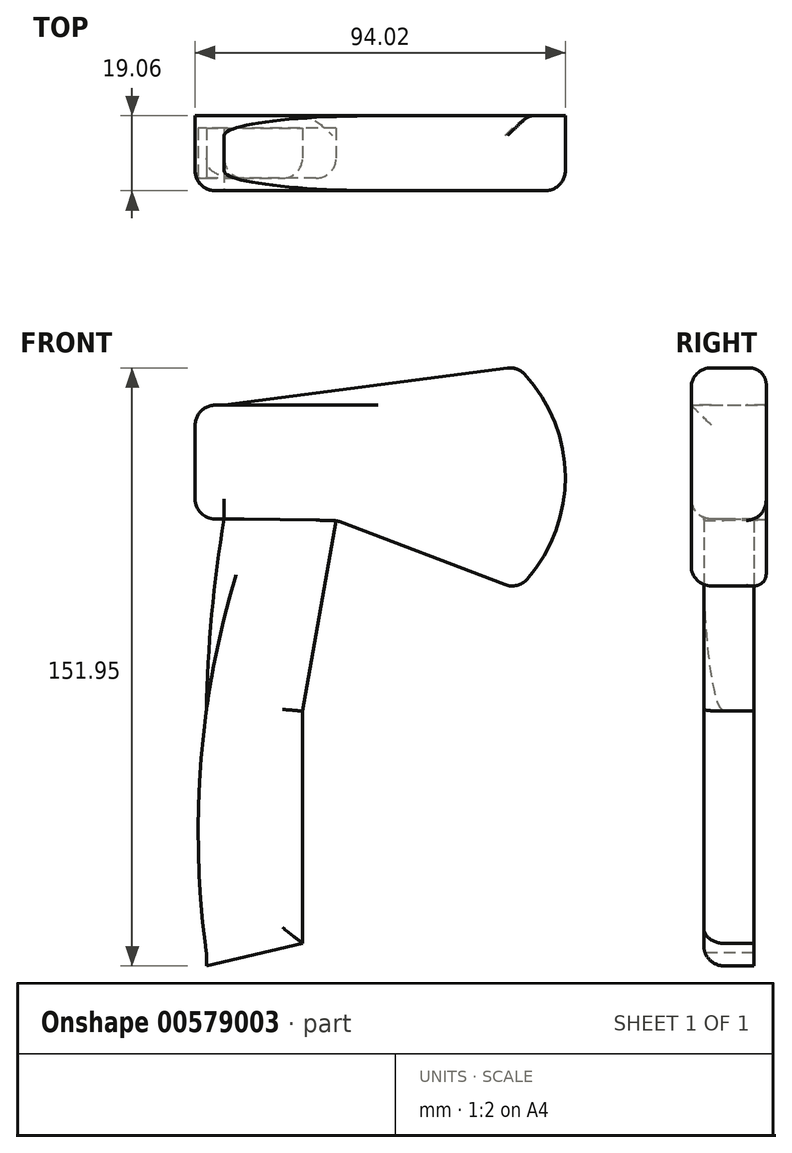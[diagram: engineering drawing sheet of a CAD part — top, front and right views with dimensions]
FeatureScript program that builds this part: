
annotation { "Feature Type Name" : "Feature", "Feature Type Description" : "" }
export const myFeature = defineFeature(function(context is Context, id is Id, definition is map)
    precondition{}
    {
        {
            var Q0;
            Q0=qCreatedBy(makeId("Front.planeOp"),FACE);
            var sketch = newSketch(context, id + "F0", { "sketchPlane" : qUnion([Q0])});
            skArc(sketch, "E0", {"start": v(-13.8, -11.12) * mm, "mid": v(-15.9, -41.85) * mm, "end": v(-13.8, -72.58) * mm});
            skLineSegment(sketch, "E1", {"start": v(-13.8, -72.58) * mm, "end": v(-13.8, -75.84) * mm});
            skArc(sketch, "E2", {"start": v(-9.33, 37.72) * mm, "mid": v(-12.45, 13.38) * mm, "end": v(-13.8, -11.12) * mm});
            skLineSegment(sketch, "E3", {"start": v(-9.33, 37.72) * mm, "end": v(-16.65, 37.72) * mm});
            skLineSegment(sketch, "E4", {"start": v(-16.65, 37.72) * mm, "end": v(-16.65, 66.62) * mm});
            skLineSegment(sketch, "E5", {"start": v(-16.65, 66.62) * mm, "end": v(-9.33, 66.62) * mm});
            skLineSegment(sketch, "E6", {"start": v(-9.33, 66.62) * mm, "end": v(65.16, 76.39) * mm});
            skLineSegment(sketch, "E7", {"start": v(19.16, 37.32) * mm, "end": v(65.16, 19.81) * mm});
            skLineSegment(sketch, "E8", {"start": v(-13.8, -75.84) * mm, "end": v(10.62, -70.14) * mm});
            skArc(sketch, "E9", {"start": v(65.16, 19.81) * mm, "mid": v(77.37, 48.1) * mm, "end": v(65.16, 76.39) * mm});
            skLineSegment(sketch, "E10", {"start": v(19.16, 37.32) * mm, "end": v(-9.33, 37.72) * mm});
            skLineSegment(sketch, "E11", {"start": v(-9.33, 66.62) * mm, "end": v(-9.33, 37.72) * mm});
            skLineSegment(sketch, "E12", {"start": v(19.16, 37.32) * mm, "end": v(19.16, 70.36) * mm});
            skLineSegment(sketch, "E13", {"start": v(10.62, -11.12) * mm, "end": v(-13.8, -11.12) * mm});
            skLineSegment(sketch, "E14", {"start": v(-1.6, -72.99) * mm, "end": v(0, -11.12) * mm});
            skLineSegment(sketch, "E15", {"start": v(19.16, 37.32) * mm, "end": v(10.62, -11.12) * mm});
            skLineSegment(sketch, "E16", {"start": v(10.62, -70.14) * mm, "end": v(10.62, -11.12) * mm});
            skLineSegment(sketch, "E17", {"start": v(0, -11.12) * mm, "end": v(4.92, 37.52) * mm});
            skSolve(sketch);
        }
        {
            var Q0;
            {var subQ1=sQuery(id+"F0.wireOp",EDGE,"E0");Q0=makeQuery(id+"F0.imprint","IMPRINT",FACE,{"disambiguationData":[TD([[makeQuery(id+"F0.imprint","IMPRINT",EDGE,{"derivedFrom":subQ1}),1.0]])]});}
            var Q1;
            {var subQ2=sQuery(id+"F0.wireOp",EDGE,"E14");Q1=makeQuery(id+"F0.imprint","IMPRINT",FACE,{"disambiguationData":[TD([[makeQuery(id+"F0.imprint","IMPRINT",EDGE,{"derivedFrom":subQ2}),-1.0]])]});}
            var Q2;
            {var subQ0=sQuery(id+"F0.wireOp",EDGE,"E2");Q2=makeQuery(id+"F0.imprint","IMPRINT",FACE,{"disambiguationData":[TD([[makeQuery(id+"F0.imprint","IMPRINT",EDGE,{"derivedFrom":subQ0}),1.0]])]});}
            var Q3;
            {var subQ0=sQuery(id+"F0.wireOp",EDGE,"E15");Q3=makeQuery(id+"F0.imprint","IMPRINT",FACE,{"disambiguationData":[TD([[makeQuery(id+"F0.imprint","IMPRINT",EDGE,{"derivedFrom":subQ0}),-1.0]])]});}
            extrude(context, id + "F1", {"entities" : qUnion([Q0, Q1, Q2, Q3]), "endBound" : BoundingType.SYMMETRIC, "oppositeDirection" : true, "depth" : 12.7 * mm, "offsetDistance" : 25.4 * mm});
        }
        {
            var Q0;
            Q0=makeQuery(id+"F0.imprint","IMPRINT",FACE,{"disambiguationData":[TD([[makeQuery(id+"F0.imprint","IMPRINT",EDGE,{"derivedFrom":sQuery(id+"F0.wireOp",EDGE,"E3")}),-1.0]])]});
            var Q1;
            {var subQ0=sQuery(id+"F0.wireOp",EDGE,"E11");Q1=makeQuery(id+"F0.imprint","IMPRINT",FACE,{"disambiguationData":[TD([[makeQuery(id+"F0.imprint","IMPRINT",EDGE,{"derivedFrom":subQ0}),1.0]])]});}
            var Q2;
            {var subQ0=sQuery(id+"F0.wireOp",EDGE,"E12");Q2=makeQuery(id+"F0.imprint","IMPRINT",FACE,{"disambiguationData":[TD([[makeQuery(id+"F0.imprint","IMPRINT",EDGE,{"derivedFrom":subQ0}),-1.0]])]});}
            extrude(context, id + "F2", {"entities" : qUnion([Q0, Q1, Q2]), "endBound" : BoundingType.SYMMETRIC, "depth" : 19.05 * mm, "offsetDistance" : 25.4 * mm});
        }
        {
            var Q0;
            Q0=makeQuery(id+"F1.opExtrude","CAP_EDGE",EDGE,{"disambiguationData":[OSD([sQuery(id+"F0.wireOp",EDGE,"E15")])],"isStart":true});
            var Q1;
            Q1=makeQuery(id+"F1.opExtrude","CAP_EDGE",EDGE,{"disambiguationData":[OSD([sQuery(id+"F0.wireOp",EDGE,"E16")])],"isStart":true});
            var Q2;
            Q2=makeQuery(id+"F1.opExtrude","CAP_EDGE",EDGE,{"disambiguationData":[OSD([sQuery(id+"F0.wireOp",EDGE,"E2")])],"isStart":true});
            var Q3;
            Q3=makeQuery(id+"F1.opExtrude","CAP_EDGE",EDGE,{"disambiguationData":[OSD([sQuery(id+"F0.wireOp",EDGE,"E8")])],"isStart":true});
            var Q4;
            Q4=makeQuery(id+"F2.opExtrude","CAP_EDGE",EDGE,{"disambiguationData":[OSD([sQuery(id+"F0.wireOp",EDGE,"E10")])],"isStart":false});
            var Q5;
            Q5=makeQuery(id+"F2.opExtrude","SWEPT_EDGE",EDGE,{"disambiguationData":[OSD([sQuery(id+"F0.wireOp",EDGE,"E3"),sQuery(id+"F0.wireOp",EDGE,"E4")])]});
            var Q6;
            Q6=makeQuery(id+"F2.opExtrude","CAP_EDGE",EDGE,{"disambiguationData":[OSD([sQuery(id+"F0.wireOp",EDGE,"E9")])],"isStart":false});
            var Q7;
            Q7=makeQuery(id+"F2.opExtrude","SWEPT_FACE",FACE,{"disambiguationData":[OSD([sQuery(id+"F0.wireOp",EDGE,"E7")])]});
            var Q8;
            Q8=makeQuery(id+"F2.opExtrude","CAP_EDGE",EDGE,{"disambiguationData":[OSD([sQuery(id+"F0.wireOp",EDGE,"E4")])],"isStart":false});
            var Q9;
            Q9=makeQuery(id+"F2.opExtrude","SWEPT_EDGE",EDGE,{"disambiguationData":[OSD([sQuery(id+"F0.wireOp",EDGE,"E4"),sQuery(id+"F0.wireOp",EDGE,"E5")])]});
            var Q10;
            Q10=makeQuery(id+"F2.opExtrude","CAP_EDGE",EDGE,{"disambiguationData":[OSD([sQuery(id+"F0.wireOp",EDGE,"E6")])],"isStart":false});
            var Q11;
            Q11=makeQuery(id+"F2.opExtrude","CAP_EDGE",EDGE,{"disambiguationData":[OSD([sQuery(id+"F0.wireOp",EDGE,"E6")])],"isStart":true});
            var Q12;
            Q12=makeQuery(id+"F2.opExtrude","SWEPT_EDGE",EDGE,{"disambiguationData":[OSD([sQuery(id+"F0.wireOp",EDGE,"E6"),sQuery(id+"F0.wireOp",EDGE,"E9")])]});
            fillet(context, id + "F3", {"entities" : qUnion([Q0, Q1, Q2, Q3, Q4, Q5, Q6, Q7, Q8, Q9, Q10, Q11, Q12]), "radius" : 5.08 * mm, "tangentPropagation" : true, "allowEdgeOverflow" : false});
        }
    });
